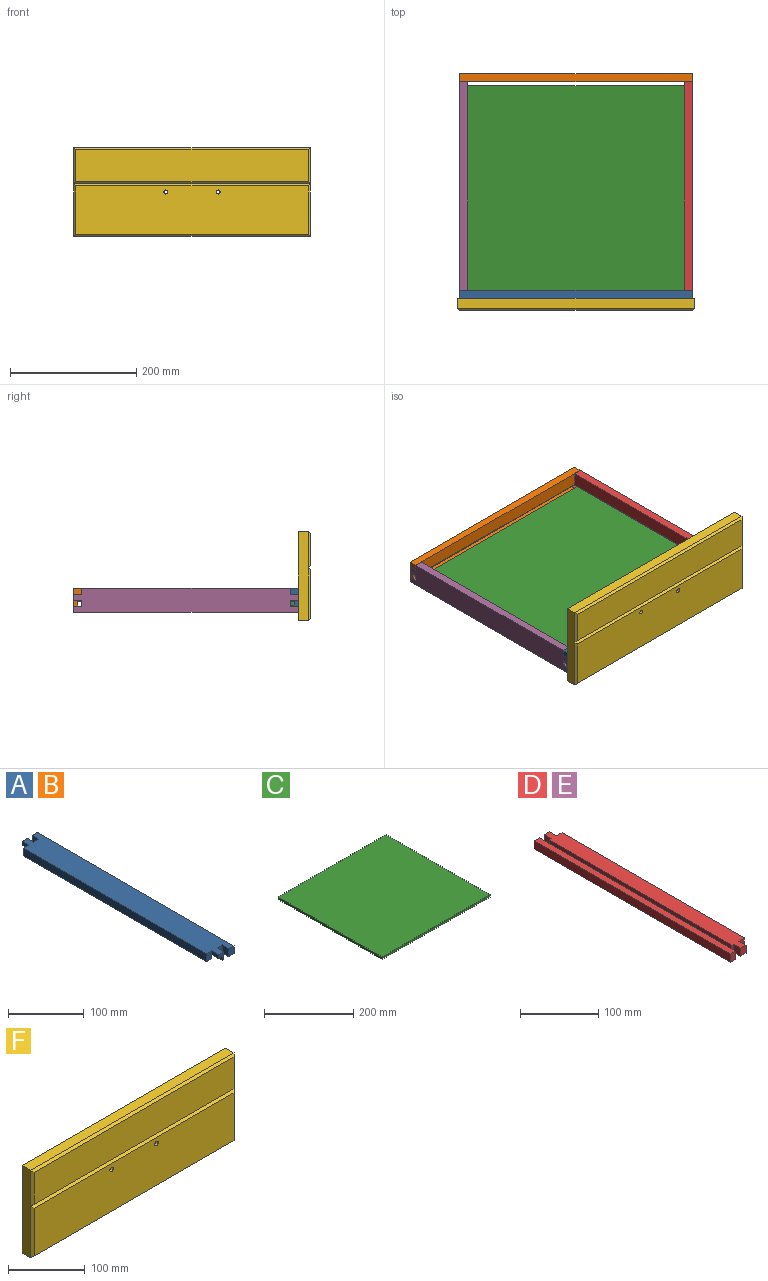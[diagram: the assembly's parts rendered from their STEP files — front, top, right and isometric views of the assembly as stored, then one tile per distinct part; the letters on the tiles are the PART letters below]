
ASSEMBLY  parts=6 mates=5
PART A: 22 faces, bbox 38.1x368.3x12.7 mm
  f0: plane 12.7x9.53mm, normal (0,-1,0), area 72.6mm2, adj f4,f5,f10,f11,f15,f20
  f1: plane 12.7x9.53mm, normal (0,1,0), area 72.6mm2, adj f4,f5,f10,f11,f12,f16
  f2: plane 342.9x12.7mm, normal (-1,0,0), area 4354.8mm2, adj f5,f6,f13,f14
  f3: plane 342.9x6.35mm, normal (1,0,0), area 2177.4mm2, adj f6,f11,f13,f14
  f4: plane 368.3x20.96mm, normal (0,0,-1), area 7475.8mm2, adj f0,f1,f7,f8,f9,f10,f16,f17
  f5: plane 368.3x38.1mm, normal (0,0,1), area 13548.4mm2, adj f0,f1,f2,f7,f8,f9,f12,f13
  f6: plane 342.9x9.53mm, normal (0,0,-1), area 3266.1mm2, adj f2,f3,f13,f14
  f7: plane 12.7x9.53mm, normal (0,-1,0), area 121mm2, adj f4,f5,f9,f19
  f8: plane 12.7x9.53mm, normal (0,1,0), area 121mm2, adj f4,f5,f9,f17
  f9: plane 368.3x12.7mm, normal (1,0,0), area 4677.4mm2, adj f4,f5,f7,f8
  f10: plane 368.3x6.35mm, normal (-1,0,0), area 2338.7mm2, adj f0,f1,f4,f11
  f11: plane 368.3x7.62mm, normal (0,0,-1), area 2806.4mm2, adj f0,f1,f3,f10,f12,f15
  f12: plane 12.7x6.35mm, normal (-1,0,0), area 80.6mm2, adj f1,f5,f11,f13
  f13: plane 12.7x9.53mm, normal (0,1,0), area 121mm2, adj f2,f3,f5,f6,f12
  f14: plane 12.7x9.53mm, normal (0,-1,0), area 121mm2, adj f2,f3,f5,f6,f15
  f15: plane 12.7x6.35mm, normal (-1,0,0), area 80.6mm2, adj f0,f5,f11,f14
  f16: plane 12.7x12.7mm, normal (1,0,0), area 161.3mm2, adj f1,f4,f5,f18
  f17: plane 12.7x12.7mm, normal (-1,0,0), area 161.3mm2, adj f4,f5,f8,f18
  f18: plane 12.7x9.53mm, normal (0,1,0), area 121mm2, adj f4,f5,f16,f17
  f19: plane 12.7x12.7mm, normal (-1,0,0), area 161.3mm2, adj f4,f5,f7,f21
  f20: plane 12.7x12.7mm, normal (1,0,0), area 161.3mm2, adj f0,f4,f5,f21
  f21: plane 12.7x9.53mm, normal (0,-1,0), area 121mm2, adj f4,f5,f19,f20
PART B: same geometry as A
PART C: 6 faces, bbox 342.9x330.2x6.4 mm
  f0: plane 342.9x6.35mm, normal (0,-1,0), area 2177.4mm2, adj f1,f3,f4,f5
  f1: plane 330.2x6.35mm, normal (1,0,0), area 2096.8mm2, adj f0,f2,f4,f5
  f2: plane 342.9x6.35mm, normal (0,1,0), area 2177.4mm2, adj f1,f3,f4,f5
  f3: plane 330.2x6.35mm, normal (-1,0,0), area 2096.8mm2, adj f0,f2,f4,f5
  f4: plane 342.9x330.2mm, normal (0,0,1), area 113225.6mm2, adj f0,f1,f2,f3
  f5: plane 342.9x330.2mm, normal (0,0,-1), area 113225.6mm2, adj f0,f1,f2,f3
PART D: 20 faces, bbox 38.1x355.6x12.7 mm
  f0: plane 330.2x12.7mm, normal (1,0,0), area 4193.5mm2, adj f3,f4,f17,f18
  f1: plane 12.7x9.53mm, normal (0,-1,0), area 121mm2, adj f3,f4,f15,f16
  f2: plane 12.7x9.53mm, normal (0,1,0), area 121mm2, adj f3,f4,f12,f19
  f3: plane 355.6x22.23mm, normal (0,0,1), area 7580.6mm2, adj f0,f1,f2,f6,f12,f13,f14,f15
  f4: plane 355.6x38.1mm, normal (0,0,-1), area 13064.5mm2, adj f0,f1,f2,f8,f9,f10,f11,f12
  f5: plane 330.2x6.35mm, normal (0,0,1), area 2096.8mm2, adj f6,f11,f13,f14
  f6: plane 330.2x6.35mm, normal (-1,0,0), area 2096.8mm2, adj f3,f5,f13,f14
  f7: plane 355.6x9.53mm, normal (0,0,1), area 3387.1mm2, adj f8,f9,f10,f11
  f8: plane 355.6x12.7mm, normal (-1,0,0), area 4516.1mm2, adj f4,f7,f9,f10
  f9: plane 12.7x9.53mm, normal (0,-1,0), area 121mm2, adj f4,f7,f8,f11
  f10: plane 12.7x9.53mm, normal (0,1,0), area 121mm2, adj f4,f7,f8,f11
  f11: plane 355.6x12.7mm, normal (1,0,0), area 2419.3mm2, adj f4,f5,f7,f9,f10,f13,f14
  f12: plane 12.7x12.7mm, normal (-1,0,0), area 161.3mm2, adj f2,f3,f4,f13
  f13: plane 12.7x9.53mm, normal (0,1,0), area 80.6mm2, adj f3,f4,f5,f6,f11,f12
  f14: plane 12.7x9.53mm, normal (0,-1,0), area 80.6mm2, adj f3,f4,f5,f6,f11,f15
  f15: plane 12.7x12.7mm, normal (-1,0,0), area 161.3mm2, adj f1,f3,f4,f14
  f16: plane 12.7x12.7mm, normal (1,0,0), area 161.3mm2, adj f1,f3,f4,f17
  f17: plane 12.7x9.53mm, normal (0,-1,0), area 121mm2, adj f0,f3,f4,f16
  f18: plane 12.7x9.53mm, normal (0,1,0), area 121mm2, adj f0,f3,f4,f19
  f19: plane 12.7x12.7mm, normal (1,0,0), area 161.3mm2, adj f2,f3,f4,f18
PART E: same geometry as D
PART F: 17 faces, bbox 374.7x19.1x139.7 mm
  f0: plane 368.3x76.2mm, normal (0,-1,0), area 28001.1mm2, adj f8,f9,f10,f11,f15,f16
  f1: plane 139.7x15.88mm, normal (1,0,0), area 2217.7mm2, adj f2,f3,f6,f11,f14
  f2: plane 374.65x15.88mm, normal (0,0,-1), area 5947.6mm2, adj f1,f4,f6,f10
  f3: plane 374.65x15.88mm, normal (0,0,1), area 5947.6mm2, adj f1,f4,f6,f13
  f4: plane 139.7x15.88mm, normal (-1,0,0), area 2217.7mm2, adj f2,f3,f6,f9,f12
  f5: plane 368.3x50.8mm, normal (0,-1,0), area 18709.6mm2, adj f7,f12,f13,f14
  f6: plane 374.65x139.7mm, normal (0,1,0), area 52275.3mm2, adj f1,f2,f3,f4,f15,f16
  f7: plane 374.65x3.18mm, normal (0,-0.71,-0.71), area 1668mm2, adj f5,f8,f12,f14
  f8: plane 374.65x3.18mm, normal (0,-0.71,0.71), area 1668mm2, adj f0,f7,f9,f11
  f9: plane 82.55x3.18mm, normal (-0.71,-0.71,0), area 356.4mm2, adj f0,f4,f8,f10
  f10: plane 374.65x3.18mm, normal (0,-0.71,-0.71), area 1668mm2, adj f0,f2,f9,f11
  f11: plane 82.55x3.18mm, normal (0.71,-0.71,0), area 356.4mm2, adj f0,f1,f8,f10
  f12: plane 57.15x3.18mm, normal (-0.71,-0.71,0), area 242.4mm2, adj f4,f5,f7,f13
  f13: plane 374.65x3.18mm, normal (0,-0.71,0.71), area 1668mm2, adj f3,f5,f12,f14
  f14: plane 57.15x3.18mm, normal (0.71,-0.71,0), area 242.4mm2, adj f1,f5,f7,f13
  f15: cylinder r=3.17mm len=19.05mm, axis (0,1,0), area 380mm2, adj f0,f6
  f16: cylinder r=3.17mm len=19.05mm, axis (0,1,0), area 380mm2, adj f0,f6
PLACE A rot(axis=(0.58,-0.58,0.58),120deg) t=(-296.55,-339.22,-301.2)mm
PLACE B rot(axis=(-0.58,-0.58,-0.58),120deg) t=(71.75,-9.02,-301.2)mm
PLACE C rot(axis=(1,0,0),180deg) t=(-112.4,-180.47,-284.69)mm
PLACE D rot(axis=(0,-1,0),90deg) t=(71.75,3.68,-301.2)mm
PLACE E rot(axis=(0.71,0,0.71),180deg) t=(-296.55,-351.92,-301.2)mm
PLACE F t=(-112.4,-351.92,-244.05)mm
MATE fastened C.f2 <-> A.f11  axis (0,-1,0) through (-112.4,-345.57,-287.87)mm
MATE fastened A.f5 <-> F.f6  axis (0,-1,0) through (-112.4,-351.92,-301.2)mm
MATE fastened E.f7 <-> B.f14  axis (1,0,0) through (-283.85,3.68,-301.2)mm
MATE fastened A.f4 <-> E.f18  axis (0,1,0) through (-296.55,-339.22,-263.1)mm
MATE fastened B.f4 <-> D.f18  axis (0,-1,0) through (71.75,-9.02,-263.1)mm
